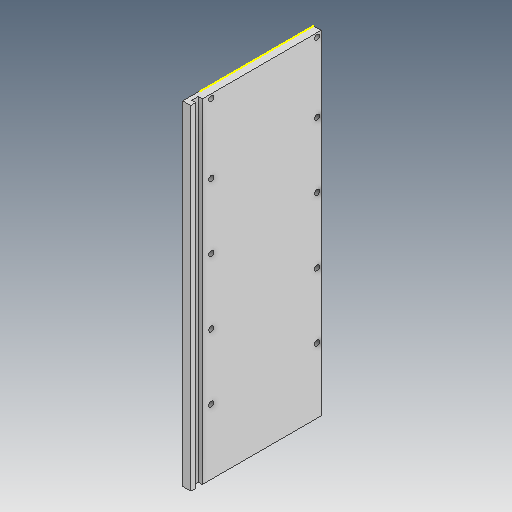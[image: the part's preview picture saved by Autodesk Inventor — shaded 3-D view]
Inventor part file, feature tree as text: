
AUTODESK INVENTOR PART (.ipt)
format: ipt  version: 2020.3 (Build 243373010, 373A)  size: 110,080 bytes
history: native  units: mm
features: other x3, sketch x3
ambient origin geometry x8: Origin, YZ Plane, XZ Plane, XY Plane, X Axis, Y Axis, Z Axis, Center Point
bodies: Solid1 (feature_tree)
feature tree (6):
  other  "SidePanel.ipt"
  other  "Solid1::SidePanel.ipt"
  other  "TaggingFeature1"
  sketch  "Sketch1"  dims[d0=10.0mm]
  sketch  "Sketch2"
  sketch  "Sketch3"
